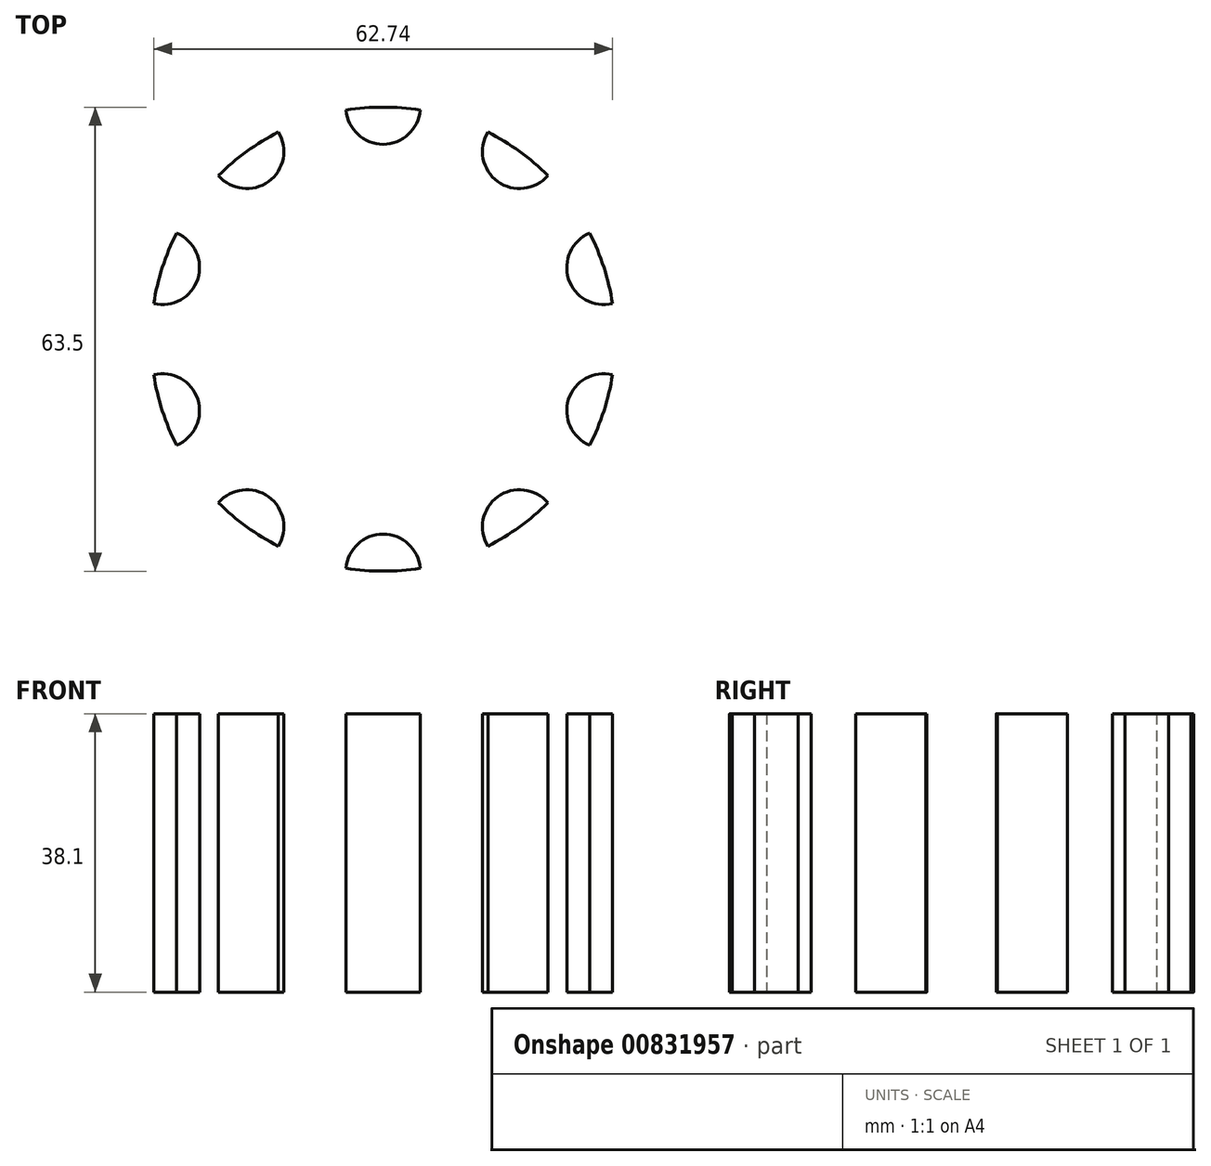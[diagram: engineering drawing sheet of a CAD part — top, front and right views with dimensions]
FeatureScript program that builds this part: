
annotation { "Feature Type Name" : "Feature", "Feature Type Description" : "" }
export const myFeature = defineFeature(function(context is Context, id is Id, definition is map)
    precondition{}
    {
        {
            var Q0;
            Q0=qCreatedBy(makeId("Top.planeOp"),FACE);
            var sketch = newSketch(context, id + "F0", { "sketchPlane" : qUnion([Q0])});
            skCircle(sketch, "E0", {"center": v(0, 0) * mm, "radius": 31.75 * mm});
            skSolve(sketch);
        }
        {
            var Q0;
            Q0=qSketchRegion(id+"F0",true);
            extrude(context, id + "F1", {"entities" : qUnion([Q0]), "depth" : 38.1 * mm});
        }
        {
            var Q0;
            Q0=qCreatedBy(makeId("Top.planeOp"),FACE);
            var sketch = newSketch(context, id + "F2", { "sketchPlane" : qUnion([Q0])});
            skCircle(sketch, "E1", {"center": v(0, 31.75) * mm, "radius": 5.08 * mm});
            skCircle(sketch, "E2.1.0", {"center": v(-18.66, 25.69) * mm, "radius": 5.08 * mm});
            skCircle(sketch, "E2.2.0", {"center": v(-30.2, 9.81) * mm, "radius": 5.08 * mm});
            skCircle(sketch, "E2.3.0", {"center": v(-30.2, -9.81) * mm, "radius": 5.08 * mm});
            skCircle(sketch, "E2.4.0", {"center": v(-18.66, -25.69) * mm, "radius": 5.08 * mm});
            skCircle(sketch, "E2.5.0", {"center": v(0, -31.75) * mm, "radius": 5.08 * mm});
            skCircle(sketch, "E2.6.0", {"center": v(18.66, -25.69) * mm, "radius": 5.08 * mm});
            skCircle(sketch, "E2.7.0", {"center": v(30.2, -9.81) * mm, "radius": 5.08 * mm});
            skCircle(sketch, "E2.8.0", {"center": v(30.2, 9.81) * mm, "radius": 5.08 * mm});
            skCircle(sketch, "E2.9.0", {"center": v(18.66, 25.69) * mm, "radius": 5.08 * mm});
            skPoint(sketch, "E2.center", {"position": v(0, 0) * mm});
            skSolve(sketch);
        }
        {
            var Q0;
            Q0=qSketchRegion(id+"F2",true);
            extrude(context, id + "F3", {"entities" : qUnion([Q0]), "operationType" : NewBodyOperationType.INTERSECT, "offsetDistance" : 25.4 * mm, "depth" : 50.8 * mm});
        }
    });
